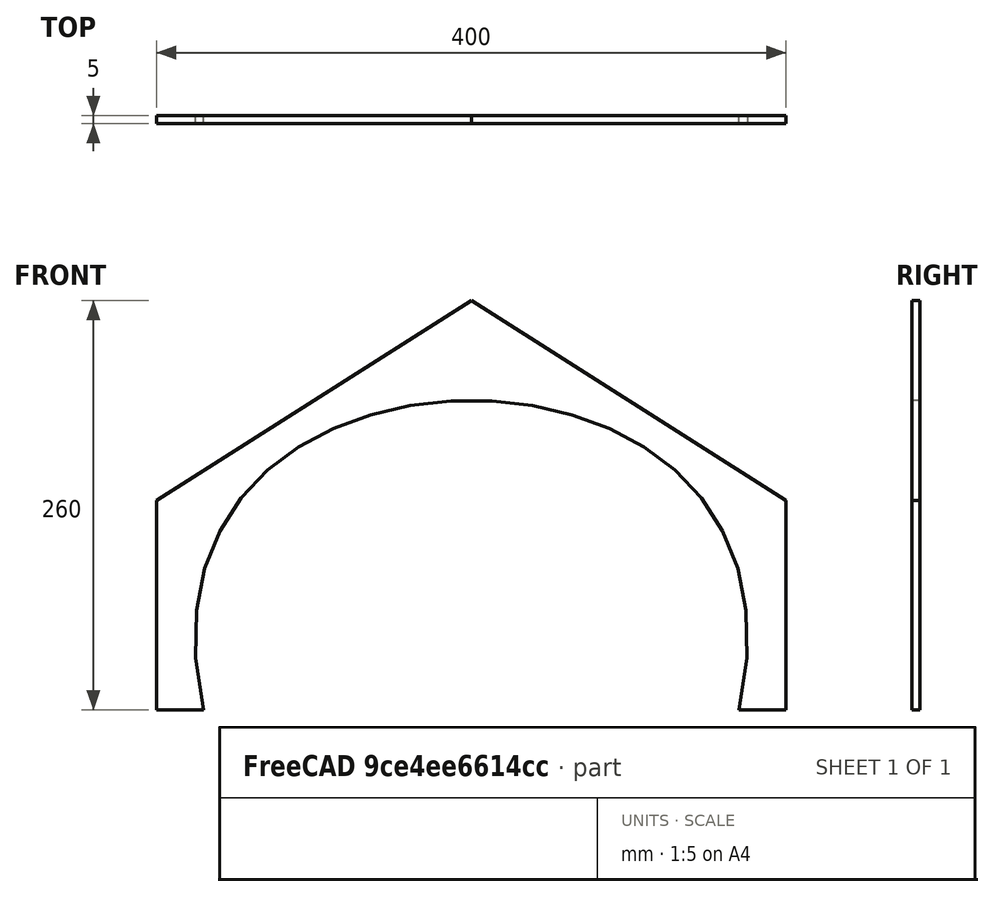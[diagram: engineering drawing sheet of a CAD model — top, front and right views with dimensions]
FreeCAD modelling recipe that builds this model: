
FCSTD DOCUMENT  (FreeCAD 0.17R11311 (Git))
Label: Vorderteil
License: All rights reserved
LicenseURL: http://en.wikipedia.org/wiki/All_rights_reserved
objects: PartDesign::Body×2, Sketcher::SketchObject×1, PartDesign::Pad×1, Part::Feature×1
note: 6 computed .brp shape members not serialized (recipe doc carries the construction recipe); baked Part::Feature solids carry a one-line shape summary decoded from their .brp

FEATURE [PartDesign::Body] Body001
  Origin = -> Body001Origin
FEATURE [Sketcher::SketchObject] Sketch
  MapMode = 5
  Placement = pos=(0,0,0) rot=(0,0.707107,0.707107;3.14159rad)
  Support = -> [XZ_Plane]
  sketch-geometry (16):
    g0: LineSegment StartX=200 StartY=0 StartZ=0 EndX=200 EndY=133 EndZ=0
    g1: LineSegment StartX=200 StartY=133 StartZ=0 EndX=0 EndY=260 EndZ=0
    g2: LineSegment StartX=0 StartY=260 StartZ=0 EndX=-200 EndY=133 EndZ=0
    g3: LineSegment StartX=-200 StartY=133 StartZ=0 EndX=-200 EndY=0 EndZ=0
    g4: LineSegment StartX=-200 StartY=0 StartZ=0 EndX=-170 EndY=0 EndZ=0
    g5: LineSegment StartX=200 StartY=0 StartZ=0 EndX=170 EndY=0 EndZ=0
    g6: Circle [constr] CenterX=-170 CenterY=0 CenterZ=0 NormalX=0 NormalY=0 NormalZ=1 Radius=23
    g7-g11: Circle [constr] x5 (B-spline internal-alignment scaffolding for g12; pole/knot coordinates omitted)
    g12: BSplineCurve PolesCount=5 KnotsCount=3 Degree=3 IsPeriodic=0
    g13: GeomPoint [constr] X=-170 Y=0 Z=0
    g14: GeomPoint [constr] X=0 Y=196.5 Z=0
    g15: GeomPoint [constr] X=170 Y=0 Z=0
  constraints (33):
    c: Coincident(g0,g1)
    c: Coincident(g1,g2)
    c: Coincident(g2,g3)
    c: PointOnObject(g3,g-1)
    c: PointOnObject(g0,g-1)
    c: Vertical(g3)
    c: Vertical(g0)
    c: Symmetric(g3,g0,g-2)
    c: PointOnObject(g1,g-2)
    c: DistanceX(g3,g0) = 400
    c: DistanceY(g3,g3) = 133
    c: Equal(g3,g0)
    c: DistanceY(g-1,g1) = 260
    c: Coincident(g4,g3)
    c: PointOnObject(g4,g-1)
    c: DistanceX(g3,g4) = 30
    c: Coincident(g5,g0)
    c: PointOnObject(g5,g-1)
    c: DistanceX(g5,g0) = 30
    c: Coincident(g6,g4)
    c: Radius(g6) = 23
    c: Radius(g7) = 27
    c: Equal(g7, g8-g11) x4
    c: InternalAlignment(g7-g11 -> g12) x5
    c: InternalAlignment(g13,g12)
    c: InternalAlignment(g14,g12)
    c: InternalAlignment(g15,g12)
    c: Coincident(g7,g4)
    c: Coincident(g11,g5)
    c: PointOnObject(g9,g-2)
    c: Coincident(g9,g1)
    c: Coincident(g8,g2)
    c: Coincident(g10,g0)
FEATURE [PartDesign::Pad] Pad
  BaseFeature = -> Sketch
  Length = 5
  Length2 = 100
  Placement = pos=(0,0,0) rot=(0,0.707107,0.707107;3.14159rad)
  Profile = -> Sketch
  Type = 0
FEATURE [PartDesign::Body] Body
  BaseFeature = -> Sketch
  Group = -> [Sketch,Pad]
  Origin = -> BodyOrigin
  Tip = -> Pad
FEATURE [Part::Feature] Pad001
  Placement = pos=(0,0,0) rot=(0,0.707107,0.707107;3.14159rad)
  shape: bbox 400 x 5 x 260 mm, 9 faces (baked)
